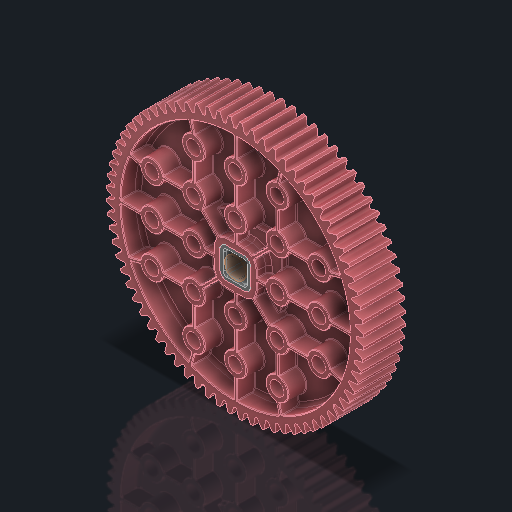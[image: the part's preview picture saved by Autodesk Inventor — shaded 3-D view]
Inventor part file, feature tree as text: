
AUTODESK INVENTOR PART (.ipt)
format: ipt  version: 2023.2 (Build 272271030, 271C)  size: 4,273,152 bytes
history: native  units: in
note: dims shown in document units (in); Inventor stores cm internally (conversion verified against a paired STEP export)
features: other x3, sketch x1, extrude x1
ambient origin geometry x8: Origin, YZ Plane, XZ Plane, XY Plane, X Axis, Y Axis, Z Axis, Center Point
bodies: Solid1 (feature_tree), Solid2 (feature_tree)
feature tree (5):
  sketch  "Sketch1"  dims[d0=0.25in d1=0.3937in d2=0.0in]
  other  "Srf1"
  other  "276-7574-001_OVERMOLD Rev4_72T 24DP Gear_1:1"
  other  "276-7573-002 Rev7_2:1"
  extrude  "ExtrusionSrf1"  Depth=0.3937in TaperAngle=0.0deg
